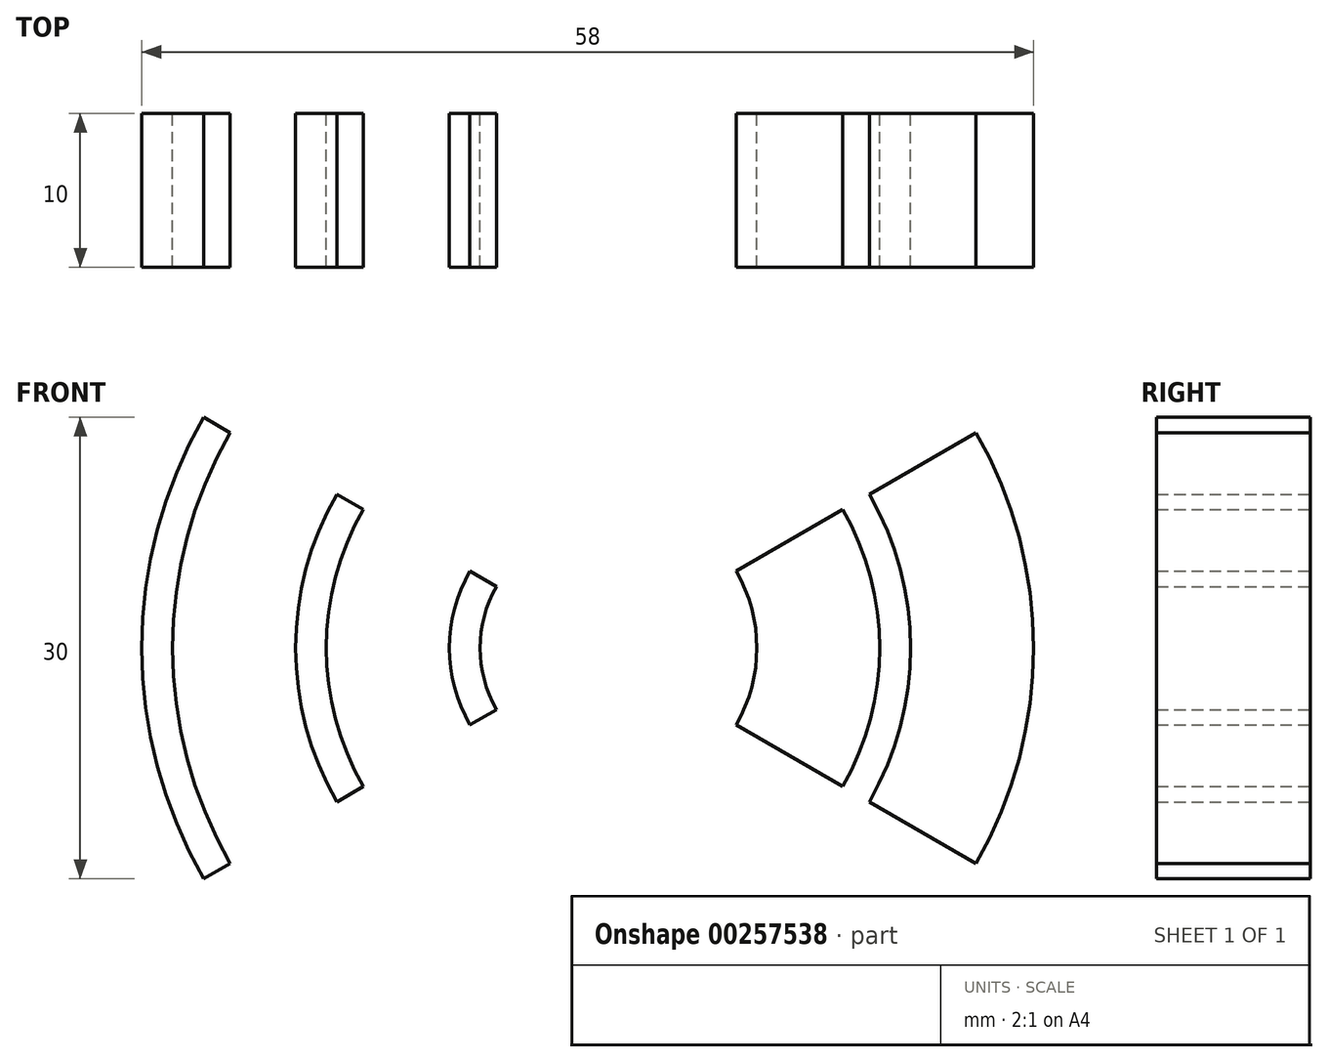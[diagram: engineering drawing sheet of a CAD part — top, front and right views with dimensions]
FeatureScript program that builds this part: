
annotation { "Feature Type Name" : "Feature", "Feature Type Description" : "" }
export const myFeature = defineFeature(function(context is Context, id is Id, definition is map)
    precondition{}
    {
        {
            var Q0;
            Q0=qCreatedBy(makeId("Front.planeOp"),FACE);
            var sketch = newSketch(context, id + "F0", { "sketchPlane" : qUnion([Q0])});
            skLineSegment(sketch, "E0", {"start": v(0, 0) * mm, "end": v(43.3, 25) * mm});
            skLineSegment(sketch, "E1", {"start": v(0, 0) * mm, "end": v(43.3, -25) * mm});
            skLineSegment(sketch, "E2", {"start": v(0, 56.4) * mm, "end": v(0, -47.25) * mm, "construction": true});
            skArc(sketch, "E3", {"start": v(17.32, 10) * mm, "mid": v(20, 0) * mm, "end": v(17.32, -10) * mm});
            skPoint(sketch, "E4.startSnap0", {"position": v(20, 0) * mm});
            skArc(sketch, "E5", {"start": v(8.66, 5) * mm, "mid": v(10, 0) * mm, "end": v(8.66, -5) * mm});
            skArc(sketch, "E6", {"start": v(25.98, 15) * mm, "mid": v(30, 0) * mm, "end": v(25.98, -15) * mm});
            skArc(sketch, "E7.0", {"start": v(24.25, 14) * mm, "mid": v(28, 0) * mm, "end": v(24.25, -14) * mm});
            skArc(sketch, "E8.0", {"start": v(15.59, 9) * mm, "mid": v(18, 0) * mm, "end": v(15.59, -9) * mm});
            skArc(sketch, "E9.0", {"start": v(6.93, 4) * mm, "mid": v(8, 0) * mm, "end": v(6.93, -4) * mm});
            skPoint(sketch, "E10.MirrorP", {"position": v(-20, 0) * mm});
            skArc(sketch, "E11.MirrorCS", {"start": v(-8.66, 5) * mm, "mid": v(-10, 0) * mm, "end": v(-8.66, -5) * mm});
            skArc(sketch, "E12.MirrorCS", {"start": v(-17.32, 10) * mm, "mid": v(-20, 0) * mm, "end": v(-17.32, -10) * mm});
            skArc(sketch, "E13.MirrorCS", {"start": v(-6.93, 4) * mm, "mid": v(-8, 0) * mm, "end": v(-6.93, -4) * mm});
            skArc(sketch, "E14.MirrorCS", {"start": v(-15.59, 9) * mm, "mid": v(-18, 0) * mm, "end": v(-15.59, -9) * mm});
            skArc(sketch, "E15.MirrorCS", {"start": v(-25.98, 15) * mm, "mid": v(-30, 0) * mm, "end": v(-25.98, -15) * mm});
            skArc(sketch, "E16.MirrorCS", {"start": v(-24.25, 14) * mm, "mid": v(-28, 0) * mm, "end": v(-24.25, -14) * mm});
            skLineSegment(sketch, "E17.MirrorCS", {"start": v(0, 0) * mm, "end": v(-43.3, 25) * mm});
            skLineSegment(sketch, "E18.MirrorCS", {"start": v(0, 0) * mm, "end": v(-43.3, -25) * mm});
            skSolve(sketch);
        }
        {
            var Q0;
            {var subQ0=sQuery(id+"F0.wireOp",EDGE,"E6");Q0=makeQuery(id+"F0.imprint","IMPRINT",FACE,{"disambiguationData":[TD([[makeQuery(id+"F0.imprint","IMPRINT",EDGE,{"derivedFrom":subQ0}),-1.0]])]});}
            var Q1;
            {var subQ0=sQuery(id+"F0.wireOp",EDGE,"E3");Q1=makeQuery(id+"F0.imprint","IMPRINT",FACE,{"disambiguationData":[TD([[makeQuery(id+"F0.imprint","IMPRINT",EDGE,{"derivedFrom":subQ0}),-1.0]])]});}
            var Q2;
            {var subQ0=sQuery(id+"F0.wireOp",EDGE,"E5");Q2=makeQuery(id+"F0.imprint","IMPRINT",FACE,{"disambiguationData":[TD([[makeQuery(id+"F0.imprint","IMPRINT",EDGE,{"derivedFrom":subQ0}),-1.0]])]});}
            var Q3;
            {var subQ0=sQuery(id+"F0.wireOp",EDGE,"E11.MirrorCS");Q3=makeQuery(id+"F0.imprint","IMPRINT",FACE,{"disambiguationData":[TD([[makeQuery(id+"F0.imprint","IMPRINT",EDGE,{"derivedFrom":subQ0}),1.0]])]});}
            var Q4;
            {var subQ0=sQuery(id+"F0.wireOp",EDGE,"E14.MirrorCS");Q4=makeQuery(id+"F0.imprint","IMPRINT",FACE,{"disambiguationData":[TD([[makeQuery(id+"F0.imprint","IMPRINT",EDGE,{"derivedFrom":subQ0}),-1.0]])]});}
            var Q5;
            {var subQ0=sQuery(id+"F0.wireOp",EDGE,"E15.MirrorCS");Q5=makeQuery(id+"F0.imprint","IMPRINT",FACE,{"disambiguationData":[TD([[makeQuery(id+"F0.imprint","IMPRINT",EDGE,{"derivedFrom":subQ0}),1.0]])]});}
            extrude(context, id + "F1", {"entities" : qUnion([Q0, Q1, Q2, Q3, Q4, Q5]), "depth" : 5 * mm, "hasSecondDirection" : true, "secondDirectionOppositeDirection" : true, "secondDirectionDepth" : 5 * mm});
        }
    });
